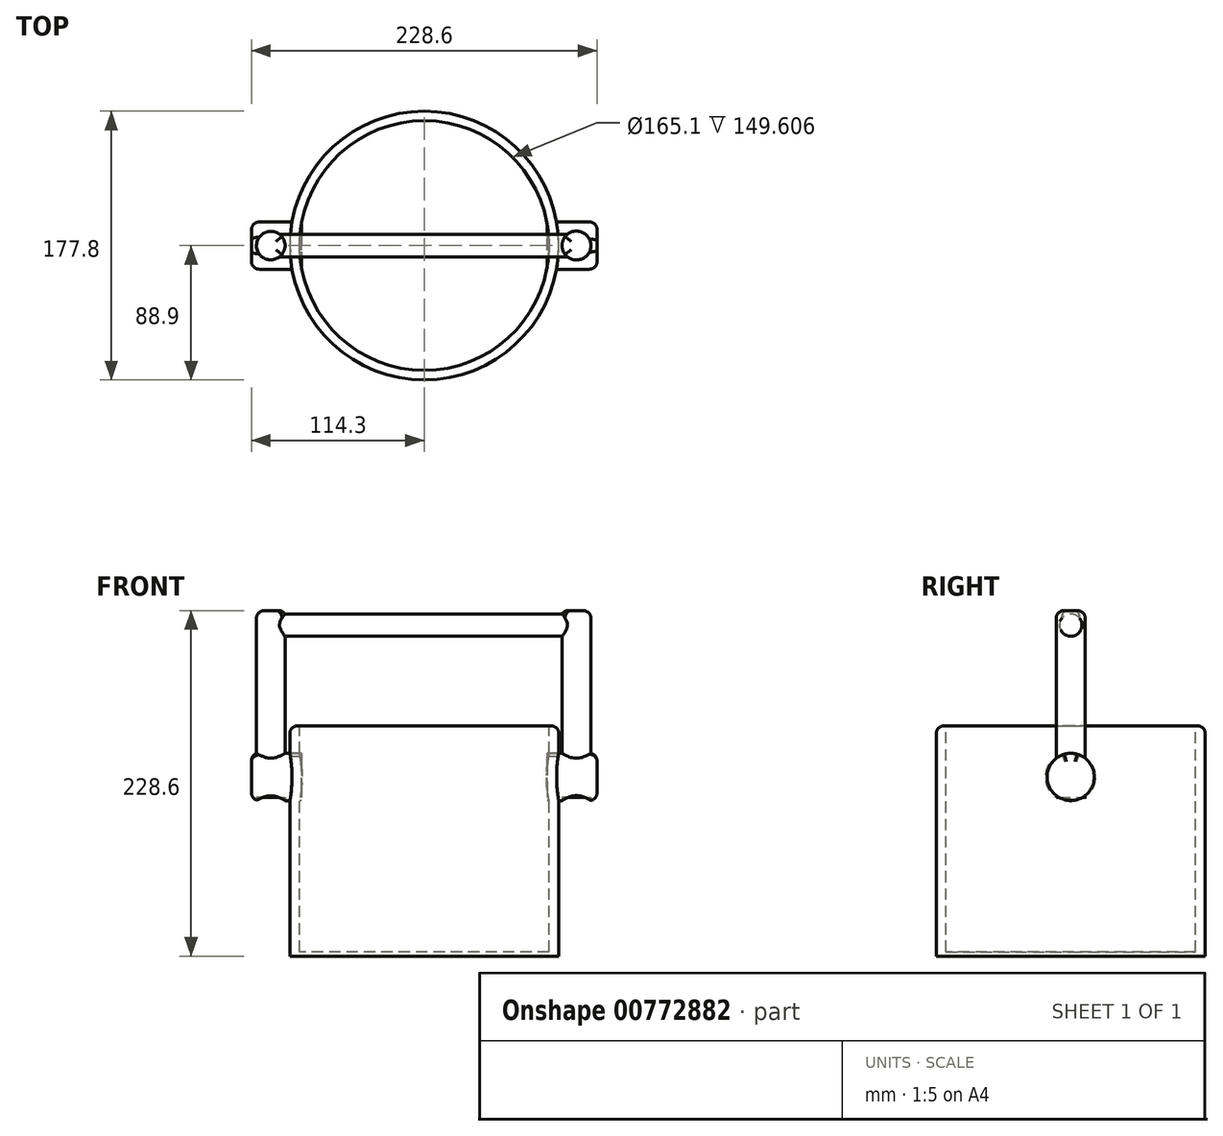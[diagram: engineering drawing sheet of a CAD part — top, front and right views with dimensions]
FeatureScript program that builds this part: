
annotation { "Feature Type Name" : "Feature", "Feature Type Description" : "" }
export const myFeature = defineFeature(function(context is Context, id is Id, definition is map)
    precondition{}
    {
        {
            var Q0;
            Q0=qCreatedBy(makeId("Top.planeOp"),FACE);
            var sketch = newSketch(context, id + "F0", { "sketchPlane" : qUnion([Q0])});
            skCircle(sketch, "E0", {"center": v(0, 0) * mm, "radius": 88.9 * mm});
            skSolve(sketch);
        }
        {
            var Q0;
            Q0=makeQuery(id+"F0.imprint","IMPRINT",FACE,{"disambiguationData":[TD([[makeQuery(id+"F0.imprint","IMPRINT",EDGE,{"derivedFrom":sQuery(id+"F0.wireOp",EDGE,"E0")}),1.0]])]});
            extrude(context, id + "F1", {"entities" : qUnion([Q0]), "depth" : 76.2 * mm, "offsetDistance" : 25.4 * mm, "hasSecondDirection" : true, "secondDirectionOppositeDirection" : true, "secondDirectionDepth" : 76.2 * mm});
        }
        {
            var Q0;
            Q0=makeQuery(id+"F1.opExtrude","CAP_FACE",FACE,{"disambiguationData":[OSD([sQuery(id+"F0.wireOp",EDGE,"E0")])],"isStart":false});
            var sketch = newSketch(context, id + "F2", { "sketchPlane" : qUnion([Q0])});
            skCircle(sketch, "E1", {"center": v(0, 0) * mm, "radius": 82.55 * mm});
            skSolve(sketch);
        }
        {
            var Q0;
            Q0=makeQuery(id+"F2.imprint","IMPRINT",FACE,{"disambiguationData":[TD([[makeQuery(id+"F2.imprint","IMPRINT",EDGE,{"derivedFrom":sQuery(id+"F2.wireOp",EDGE,"E1")}),1.0]])]});
            extrude(context, id + "F3", {"entities" : qUnion([Q0]), "operationType" : NewBodyOperationType.REMOVE, "oppositeDirection" : true, "depth" : 149.6 * mm, "offsetDistance" : 25.4 * mm});
        }
        {
            var Q0;
            Q0=qCreatedBy(makeId("Right.planeOp"),FACE);
            var sketch = newSketch(context, id + "F4", { "sketchPlane" : qUnion([Q0])});
            skCircle(sketch, "E2", {"center": v(0, 43.02) * mm, "radius": 15.02 * mm});
            skSolve(sketch);
        }
        {
            var Q0;
            Q0 = qSketchRegion(id + "F4", true);
            extrude(context, id + "F5", {"entities" : qUnion([Q0]), "operationType" : NewBodyOperationType.REMOVE, "surfaceOperationType" : NewSurfaceOperationType.ADD, "endBound" : BoundingType.THROUGH_ALL, "oppositeDirection" : true, "depth" : 25.4 * mm, "offsetDistance" : 25.4 * mm, "hasSecondDirection" : true, "secondDirectionOppositeDirection" : false, "secondDirectionDepth" : 95 * mm});
        }
        {
            var Q0;
            Q0=qCreatedBy(makeId("Right.planeOp"),FACE);
            var sketch = newSketch(context, id + "F6", { "sketchPlane" : qUnion([Q0])});
            skCircle(sketch, "E3", {"center": v(0, 42.31) * mm, "radius": 15.63 * mm});
            skSolve(sketch);
        }
        {
            var Q0;
            Q0 = qSketchRegion(id + "F6", true);
            extrude(context, id + "F7", {"entities" : qUnion([Q0]), "operationType" : NewBodyOperationType.ADD, "surfaceOperationType" : NewSurfaceOperationType.ADD, "depth" : 114.3 * mm, "offsetDistance" : 25.4 * mm, "hasSecondDirection" : true, "secondDirectionOppositeDirection" : true, "secondDirectionDepth" : 114.3 * mm});
        }
        {
            var Q0;
            Q0=qCreatedBy(makeId("Right.planeOp"),FACE);
            var sketch = newSketch(context, id + "F8", { "sketchPlane" : qUnion([Q0])});
            skCircle(sketch, "E4", {"center": v(-0.17, 42.23) * mm, "radius": 16.62 * mm});
            skPoint(sketch, "E4.first.point", {"position": v(8.02, 56.69) * mm});
            skPoint(sketch, "E4.second.point", {"position": v(6.91, 27.2) * mm});
            skPoint(sketch, "E4.third.point", {"position": v(-14.29, 33.46) * mm});
            skSolve(sketch);
        }
        {
            var Q0;
            Q0 = qSketchRegion(id + "F8", true);
            extrude(context, id + "F9", {"entities" : qUnion([Q0]), "operationType" : NewBodyOperationType.REMOVE, "oppositeDirection" : true, "depth" : 81.28 * mm, "offsetDistance" : 25.4 * mm, "hasSecondDirection" : true, "secondDirectionOppositeDirection" : false, "secondDirectionDepth" : 81.28 * mm});
        }
        {
            var Q0;
            Q0=qCreatedBy(makeId("Top.planeOp"),FACE);
            var sketch = newSketch(context, id + "F10", { "sketchPlane" : qUnion([Q0])});
            skCircle(sketch, "E5", {"center": v(-101.57, 0) * mm, "radius": 9.43 * mm});
            skSolve(sketch);
        }
        {
            var Q0;
            Q0 = qSketchRegion(id + "F10", true);
            extrude(context, id + "F11", {"entities" : qUnion([Q0]), "operationType" : NewBodyOperationType.ADD, "surfaceOperationType" : NewSurfaceOperationType.ADD, "depth" : 152.4 * mm, "offsetDistance" : 25.4 * mm});
        }
        {
            var Q0;
            Q0=makeQuery(id+"F11.opExtrude","CAP_FACE",FACE,{"disambiguationData":[OSD([sQuery(id+"F10.wireOp",EDGE,"E5")])],"isStart":true});
            extrude(context, id + "F12", {"entities" : qUnion([Q0]), "operationType" : NewBodyOperationType.REMOVE, "oppositeDirection" : true, "depth" : 28.7 * mm, "offsetDistance" : 25.4 * mm});
        }
        {
            var Q0;
            Q0=qCreatedBy(makeId("Top.planeOp"),FACE);
            var sketch = newSketch(context, id + "F13", { "sketchPlane" : qUnion([Q0])});
            skCircle(sketch, "E6", {"center": v(100.69, 0) * mm, "radius": 9.55 * mm});
            skSolve(sketch);
        }
        {
            var Q0;
            Q0 = qSketchRegion(id + "F13", true);
            extrude(context, id + "F14", {"entities" : qUnion([Q0]), "operationType" : NewBodyOperationType.ADD, "depth" : 152.4 * mm, "offsetDistance" : 25.4 * mm});
        }
        {
            var Q0;
            Q0=makeQuery(id+"F14.opExtrude","CAP_FACE",FACE,{"disambiguationData":[OSD([sQuery(id+"F13.wireOp",EDGE,"E6")])],"isStart":true});
            extrude(context, id + "F15", {"entities" : qUnion([Q0]), "operationType" : NewBodyOperationType.REMOVE, "oppositeDirection" : true, "depth" : 28.7 * mm, "offsetDistance" : 25.4 * mm});
        }
        {
            var Q0;
            Q0=qCreatedBy(makeId("Right.planeOp"),FACE);
            var sketch = newSketch(context, id + "F16", { "sketchPlane" : qUnion([Q0])});
            skCircle(sketch, "E7", {"center": v(0, 142.77) * mm, "radius": 7.44 * mm});
            skSolve(sketch);
        }
        {
            var Q0;
            Q0 = qSketchRegion(id + "F16", true);
            extrude(context, id + "F17", {"entities" : qUnion([Q0]), "operationType" : NewBodyOperationType.ADD, "depth" : 101.6 * mm, "offsetDistance" : 25.4 * mm, "hasSecondDirection" : true, "secondDirectionOppositeDirection" : true, "secondDirectionDepth" : 101.6 * mm});
        }
        {
            var Q0;
            Q0=makeQuery(id+"F11.opExtrude","CAP_EDGE",EDGE,{"disambiguationData":[OSD([sQuery(id+"F10.wireOp",EDGE,"E5")])],"isStart":false});
            var Q1;
            Q1=makeQuery(id+"F14.opExtrude","CAP_EDGE",EDGE,{"disambiguationData":[OSD([sQuery(id+"F13.wireOp",EDGE,"E6")])],"isStart":false});
            var Q2;
            Q2=makeQuery(id+"F7.opExtrude","CAP_EDGE",EDGE,{"disambiguationData":[OSD([sQuery(id+"F6.wireOp",EDGE,"E3")])],"isStart":false});
            var Q3;
            Q3=makeQuery(id+"F7.opExtrude","CAP_EDGE",EDGE,{"disambiguationData":[OSD([sQuery(id+"F6.wireOp",EDGE,"E3")])],"isStart":true});
            var Q4;
            Q4=makeQuery(id+"F1.opExtrude","CAP_EDGE",EDGE,{"disambiguationData":[OSD([sQuery(id+"F0.wireOp",EDGE,"E0")])],"isStart":false});
            fillet(context, id + "F18", {"entities" : qUnion([Q0, Q1, Q2, Q3, Q4]), "radius" : 5.08 * mm, "tangentPropagation" : true, "allowEdgeOverflow" : false});
        }
    });
